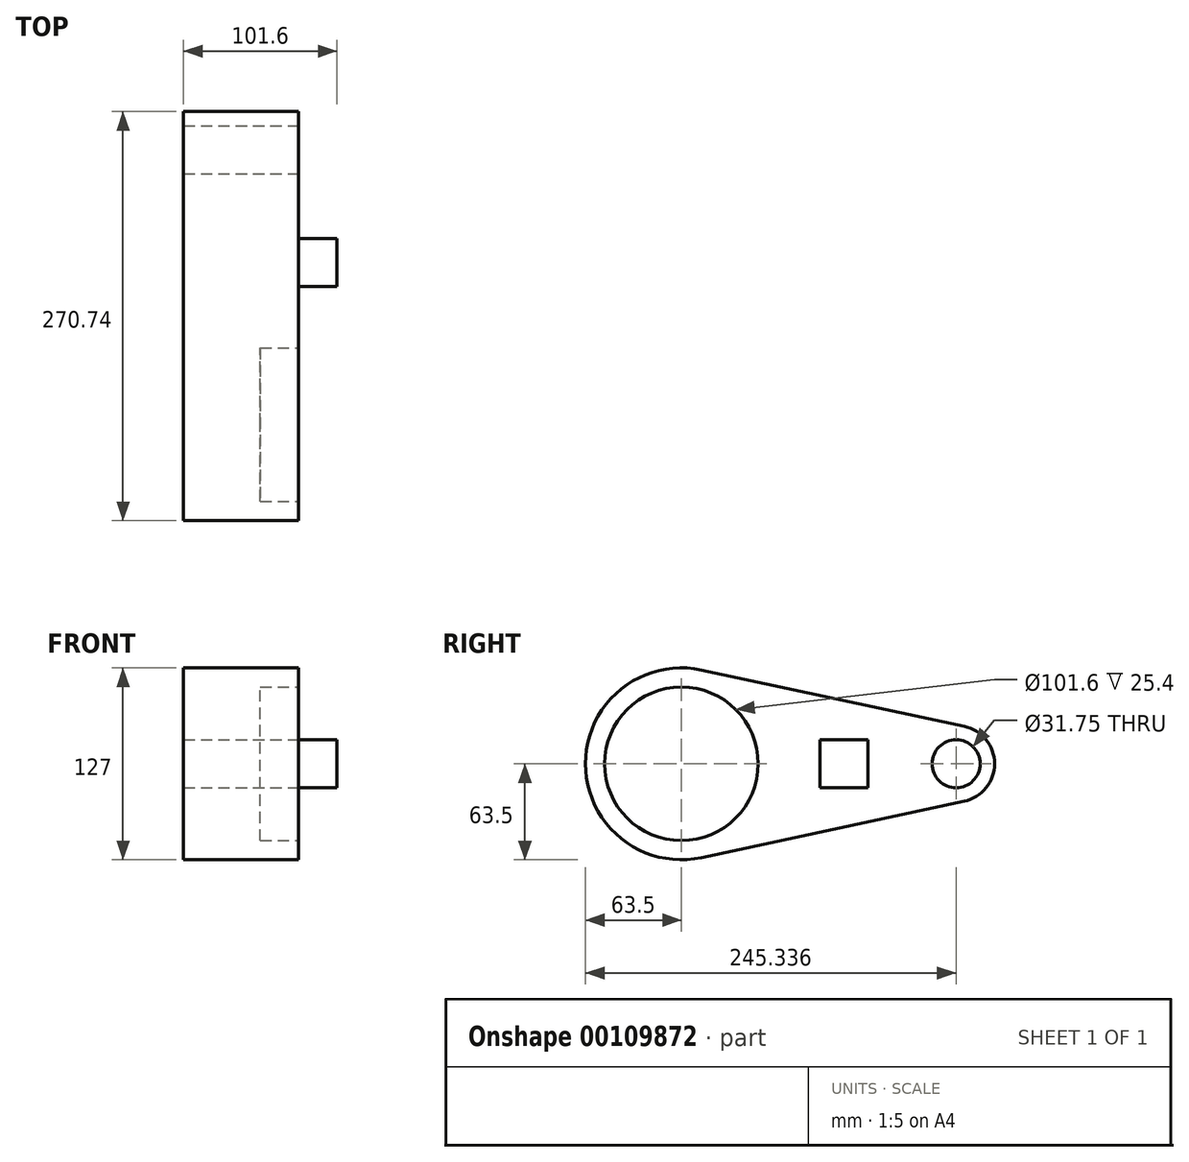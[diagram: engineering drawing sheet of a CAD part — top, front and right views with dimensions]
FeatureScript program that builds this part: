
annotation { "Feature Type Name" : "Feature", "Feature Type Description" : "" }
export const myFeature = defineFeature(function(context is Context, id is Id, definition is map)
    precondition{}
    {
        {
            var Q0;
            Q0=qCreatedBy(makeId("Right.planeOp"),FACE);
            var sketch = newSketch(context, id + "F0", { "sketchPlane" : qUnion([Q0])});
            skCircle(sketch, "E0", {"center": v(0, 0) * mm, "radius": 63.5 * mm});
            skCircle(sketch, "E1", {"center": v(181.84, 0) * mm, "radius": 25.4 * mm});
            skLineSegment(sketch, "E2", {"start": v(13.3, 62.1) * mm, "end": v(187.16, 24.84) * mm});
            skLineSegment(sketch, "E3", {"start": v(13.3, -62.1) * mm, "end": v(187.16, -24.84) * mm});
            skSolve(sketch);
        }
        {
            var Q0;
            Q0 = qSketchRegion(id + "F0", true);
            extrude(context, id + "F1", {"entities" : qUnion([Q0]), "depth" : 76.2 * mm});
        }
        {
            var Q0;
            Q0=makeQuery(id+"F1.opExtrude","CAP_FACE",FACE,{"disambiguationData":[OSD([sQuery(id+"F0.wireOp",EDGE,"E0"),sQuery(id+"F0.wireOp",EDGE,"E1"),sQuery(id+"F0.wireOp",EDGE,"E2"),sQuery(id+"F0.wireOp",EDGE,"E3")])],"isStart":false});
            var sketch = newSketch(context, id + "F2", { "sketchPlane" : qUnion([Q0])});
            skCircle(sketch, "E4", {"center": v(0, 0) * mm, "radius": 50.8 * mm});
            skSolve(sketch);
        }
        {
            var Q0;
            {var subQ0=sQuery(id+"F2.wireOp",EDGE,"E4");var subQ1=makeQuery(id+"F2.imprint","INTERSECT",VERTEX,{"derivedFrom":[makeQuery(id+"F1.opExtrude","CAP_EDGE",EDGE,{"disambiguationData":[OSD([sQuery(id+"F0.wireOp",EDGE,"E2")])],"isStart":false}),subQ0]});Q0=makeQuery(id+"F2.imprint","IMPRINT",FACE,{"disambiguationData":[TD([[makeQuery(id+"F2.imprint","IMPRINT",EDGE,{"disambiguationData":[TD([[subQ1,-1.0]])],"derivedFrom":subQ0}),1.0]])]});}
            extrude(context, id + "F3", {"entities" : qUnion([Q0]), "operationType" : NewBodyOperationType.REMOVE, "oppositeDirection" : true, "depth" : 25.4 * mm});
        }
        {
            var Q0;
            Q0=makeQuery(id+"F2.imprint","IMPRINT",FACE,{"disambiguationData":[TD([[makeQuery(id+"F2.imprint","IMPRINT",EDGE,{"derivedFrom":sQuery(id+"F2.wireOp",EDGE,"E4")}),-1.0]])]});
            var sketch = newSketch(context, id + "F4", { "sketchPlane" : qUnion([Q0])});
            skLineSegment(sketch, "E5.bottom", {"start": v(91.62, 15.88) * mm, "end": v(123.37, 15.88) * mm});
            skLineSegment(sketch, "E5.top", {"start": v(91.62, -15.88) * mm, "end": v(123.37, -15.88) * mm});
            skLineSegment(sketch, "E5.left", {"start": v(91.62, 15.88) * mm, "end": v(91.62, -15.88) * mm});
            skLineSegment(sketch, "E5.right", {"start": v(123.37, 15.87) * mm, "end": v(123.37, -15.88) * mm});
            skSolve(sketch);
        }
        {
            var Q0;
            Q0 = qSketchRegion(id + "F4", true);
            extrude(context, id + "F5", {"entities" : qUnion([Q0]), "operationType" : NewBodyOperationType.ADD, "depth" : 25.4 * mm});
        }
        {
            var Q0;
            Q0=makeQuery(id+"F2.imprint","IMPRINT",FACE,{"disambiguationData":[TD([[makeQuery(id+"F2.imprint","IMPRINT",EDGE,{"derivedFrom":sQuery(id+"F2.wireOp",EDGE,"E4")}),-1.0]])]});
            var sketch = newSketch(context, id + "F6", { "sketchPlane" : qUnion([Q0])});
            skCircle(sketch, "E6", {"center": v(181.84, 0) * mm, "radius": 15.88 * mm});
            skSolve(sketch);
        }
        {
            var Q0;
            Q0 = qSketchRegion(id + "F6", true);
            var Q1;
            Q1=makeQuery(id+"F1.opExtrude","CAP_FACE",FACE,{"disambiguationData":[OSD([sQuery(id+"F0.wireOp",EDGE,"E0"),sQuery(id+"F0.wireOp",EDGE,"E1"),sQuery(id+"F0.wireOp",EDGE,"E2"),sQuery(id+"F0.wireOp",EDGE,"E3")])],"isStart":true});
            extrude(context, id + "F7", {"entities" : qUnion([Q0]), "operationType" : NewBodyOperationType.REMOVE, "endBound" : BoundingType.UP_TO_SURFACE, "oppositeDirection" : true, "endBoundEntityFace" : qUnion([Q1]), "depth" : 25.4 * mm});
        }
    });
